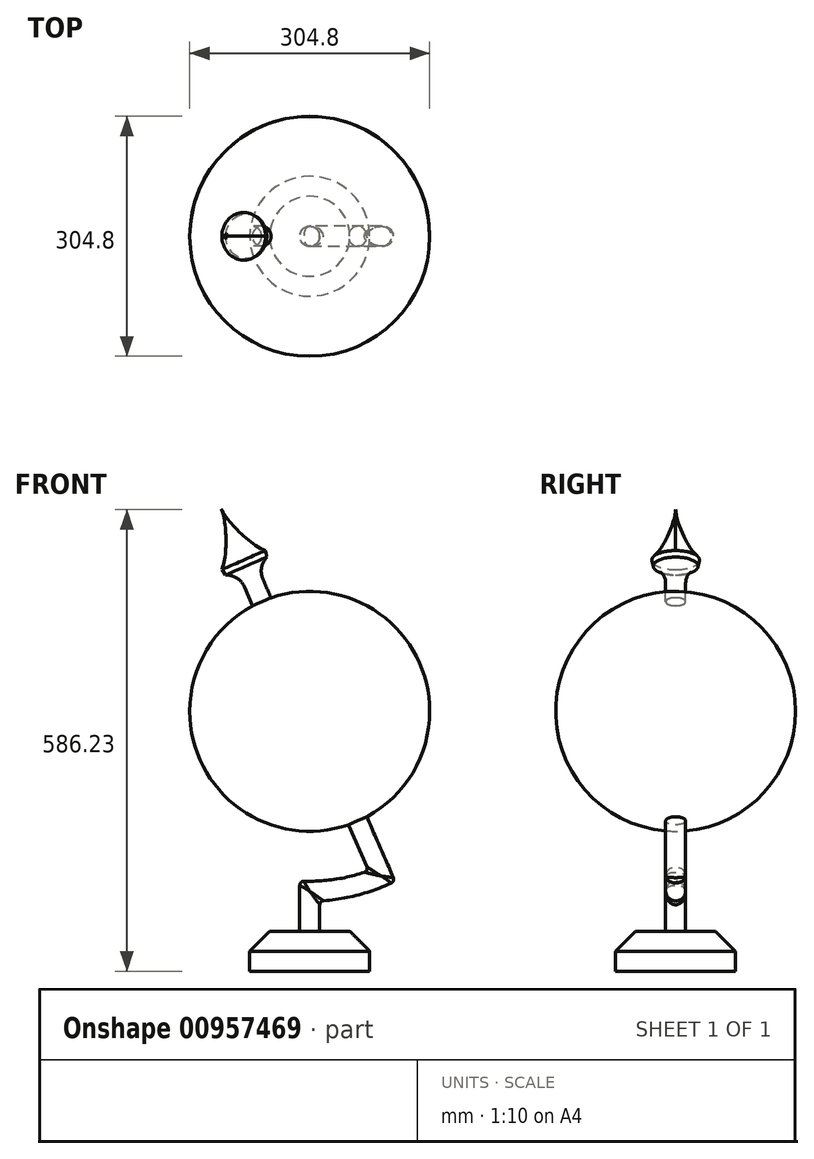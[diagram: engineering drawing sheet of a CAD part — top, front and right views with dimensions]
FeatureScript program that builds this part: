
annotation { "Feature Type Name" : "Feature", "Feature Type Description" : "" }
export const myFeature = defineFeature(function(context is Context, id is Id, definition is map)
    precondition{}
    {
        {
            var Q0;
            Q0=qCreatedBy(makeId("Front.planeOp"),FACE);
            var sketch = newSketch(context, id + "F0", { "sketchPlane" : qUnion([Q0])});
            skLineSegment(sketch, "E0", {"start": v(-152.4, 0) * mm, "end": v(152.4, 0) * mm});
            skArc(sketch, "E1", {"start": v(152.4, 0) * mm, "mid": v(0, 152.4) * mm, "end": v(-152.4, 0) * mm});
            skSolve(sketch);
        }
        {
            var Q0;
            Q0=makeQuery(id+"F0.imprint","IMPRINT",FACE,{"disambiguationData":[TD([[makeQuery(id+"F0.imprint","IMPRINT",EDGE,{"derivedFrom":sQuery(id+"F0.wireOp",EDGE,"E0")}),1.0]])]});
            var Q1;
            Q1=sQuery(id+"F0.wireOp",EDGE,"E0");
            revolve(context, id + "F1", {"surfaceOperationType" : NewSurfaceOperationType.NEW, "entities" : qUnion([Q0]), "axis" : qUnion([Q1]), "revolveType" : RevolveType.FULL});
        }
        {
            var Q0;
            Q0=qCreatedBy(makeId("Front.planeOp"),FACE);
            var sketch = newSketch(context, id + "F2", { "sketchPlane" : qUnion([Q0])});
            skLineSegment(sketch, "E2", {"start": v(0, 0) * mm, "end": v(0, 152.4) * mm, "construction": true});
            skLineSegment(sketch, "E3", {"start": v(-91.52, 209.48) * mm, "end": v(91.52, -209.48) * mm});
            skArc(sketch, "E4", {"start": v(91.52, -209.48) * mm, "mid": v(46.75, -223.77) * mm, "end": v(0, -228.6) * mm});
            skLineSegment(sketch, "E5", {"start": v(0, -228.6) * mm, "end": v(0, -330.2) * mm});
            skLineSegment(sketch, "E6.bottom", {"start": v(0, -330.2) * mm, "end": v(-76.2, -330.2) * mm});
            skLineSegment(sketch, "E6.top", {"start": v(0, -279.4) * mm, "end": v(-76.2, -279.4) * mm});
            skLineSegment(sketch, "E6.left", {"start": v(0, -330.2) * mm, "end": v(0, -279.4) * mm});
            skLineSegment(sketch, "E6.right", {"start": v(-76.2, -330.2) * mm, "end": v(-76.2, -279.4) * mm});
            skSolve(sketch);
        }
        {
            var Q0;
            Q0=makeQuery(id+"F2.imprint","IMPRINT",FACE,{"disambiguationData":[TD([[makeQuery(id+"F2.imprint","IMPRINT",EDGE,{"derivedFrom":sQuery(id+"F2.wireOp",EDGE,"E6.bottom")}),-1.0]])]});
            var Q1;
            Q1=sQuery(id+"F2.wireOp",EDGE,"E5");
            revolve(context, id + "F3", {"surfaceOperationType" : NewSurfaceOperationType.NEW, "entities" : qUnion([Q0]), "axis" : qUnion([Q1]), "revolveType" : RevolveType.FULL});
        }
        {
            var Q0;
            Q0=makeQuery(id+"F3.opRevolve","SWEPT_FACE",FACE,{"disambiguationData":[OSD([sQuery(id+"F2.wireOp",EDGE,"E6.top")])]});
            var sketch = newSketch(context, id + "F4", { "sketchPlane" : qUnion([Q0])});
            skCircle(sketch, "E7", {"center": v(0, 0) * mm, "radius": 12.7 * mm});
            skSolve(sketch);
        }
        {
            var Q0;
            Q0=makeQuery(id+"F4.imprint","IMPRINT",FACE,{"disambiguationData":[TD([[makeQuery(id+"F4.imprint","IMPRINT",EDGE,{"derivedFrom":sQuery(id+"F4.wireOp",EDGE,"E7")}),1.0]])]});
            var Q1;
            Q1=sQuery(id+"F2.wireOp",EDGE,"E5");
            var Q2;
            Q2=sQuery(id+"F2.wireOp",EDGE,"E4");
            var Q3;
            Q3=sQuery(id+"F2.wireOp",EDGE,"E3");
            sweep(context, id + "F5", {"operationType" : NewBodyOperationType.ADD, "profiles" : qUnion([Q0]), "path" : qUnion([Q1, Q2, Q3])});
        }
        {
            var Q0;
            Q0=qCreatedBy(makeId("Front.planeOp"),FACE);
            var sketch = newSketch(context, id + "F6", { "sketchPlane" : qUnion([Q0])});
            skLineSegment(sketch, "E8", {"start": v(-91.52, 209.48) * mm, "end": v(-111.86, 256.03) * mm});
            skFitSpline(sketch, "E9", {"points": [v(-111.86, 256.03) * mm, v(-46.44, 201.46) * mm], "startDerivative": vector(17.5, -40.06) * mm, "endDerivative": vector(75.42, -9.58) * mm});
            skLineSegment(sketch, "E10", {"start": v(-46.44, 201.46) * mm, "end": v(-81.35, 186.2) * mm});
            skLineSegment(sketch, "E11", {"start": v(-81.35, 186.2) * mm, "end": v(-91.52, 209.48) * mm});
            skSolve(sketch);
        }
        {
            var Q0;
            Q0=makeQuery(id+"F6.imprint","IMPRINT",FACE,{"disambiguationData":[TD([[makeQuery(id+"F6.imprint","IMPRINT",EDGE,{"derivedFrom":sQuery(id+"F6.wireOp",EDGE,"E8")}),-1.0]])]});
            var Q1;
            Q1=sQuery(id+"F6.wireOp",EDGE,"E8");
            revolve(context, id + "F7", {"operationType" : NewBodyOperationType.ADD, "surfaceOperationType" : NewSurfaceOperationType.NEW, "entities" : qUnion([Q0]), "axis" : qUnion([Q1]), "revolveType" : RevolveType.FULL});
        }
        {
            var Q0;
            Q0=makeQuery(id+"F7.boolean.opBoolean","INTERSECT",EDGE,{"derivedFrom":[makeQuery(id+"F5.opSweep","SWEPT_FACE",FACE,{"disambiguationData":[OSD([sQuery(id+"F2.wireOp",EDGE,"E3"),sQuery(id+"F4.wireOp",EDGE,"E7")])]}),makeQuery(id+"F7.opRevolve","SWEPT_FACE",FACE,{"disambiguationData":[OSD([sQuery(id+"F6.wireOp",EDGE,"E10")])]})]});
            fillet(context, id + "F8", {"entities" : qUnion([Q0]), "radius" : 25.4 * mm, "tangentPropagation" : true, "allowEdgeOverflow" : false});
        }
        {
            var Q0;
            Q0=makeQuery(id+"F3.opRevolve","SWEPT_EDGE",EDGE,{"disambiguationData":[OSD([sQuery(id+"F2.wireOp",EDGE,"E6.top"),sQuery(id+"F2.wireOp",EDGE,"E6.right")])]});
            chamfer(context, id + "F9", {"entities" : qUnion([Q0]), "width" : 25.4 * mm, "tangentPropagation" : true});
        }
        {
            var Q0;
            Q0=makeQuery(id+"F5.opSweep","MID_CAP_EDGE",EDGE,{"disambiguationData":[OSD([sQuery(id+"F2.wireOp",VERTEX,"E3.end"),sQuery(id+"F4.wireOp",EDGE,"E7")]),OD(1.0)],"capPos":2.0});
            var Q1;
            Q1=makeQuery(id+"F5.opSweep","MID_CAP_EDGE",EDGE,{"disambiguationData":[OSD([sQuery(id+"F2.wireOp",VERTEX,"E4.end"),sQuery(id+"F4.wireOp",EDGE,"E7")]),OD(0.0)],"capPos":1.0});
            var Q2;
            Q2=makeQuery(id+"F5.opSweep","MID_CAP_EDGE",EDGE,{"disambiguationData":[OSD([sQuery(id+"F2.wireOp",VERTEX,"E4.end"),sQuery(id+"F4.wireOp",EDGE,"E7")]),OD(1.0)],"capPos":1.0});
            var Q3;
            Q3=makeQuery(id+"F5.opSweep","MID_CAP_EDGE",EDGE,{"disambiguationData":[OSD([sQuery(id+"F2.wireOp",VERTEX,"E3.end"),sQuery(id+"F4.wireOp",EDGE,"E7")]),OD(0.0)],"capPos":2.0});
            fillet(context, id + "F10", {"entities" : qUnion([Q0, Q1, Q2, Q3]), "radius" : 5.08 * mm, "tangentPropagation" : true, "allowEdgeOverflow" : false});
        }
        {
            var Q0;
            Q0=makeQuery(id+"F8.opFillet","BLEND_EDGE",EDGE,{"blendedFrom":[makeQuery(id+"F7.boolean.opBoolean","INTERSECT",EDGE,{"derivedFrom":[makeQuery(id+"F5.opSweep","SWEPT_FACE",FACE,{"disambiguationData":[OSD([sQuery(id+"F2.wireOp",EDGE,"E3"),sQuery(id+"F4.wireOp",EDGE,"E7")])]}),makeQuery(id+"F7.opRevolve","SWEPT_FACE",FACE,{"disambiguationData":[OSD([sQuery(id+"F6.wireOp",EDGE,"E10")])]})]}),makeQuery(id+"F7.opRevolve","SWEPT_FACE",FACE,{"disambiguationData":[OSD([sQuery(id+"F6.wireOp",EDGE,"E9")])]})],"blendedInto":[makeQuery(id+"F7.opRevolve","SWEPT_FACE",FACE,{"disambiguationData":[OSD([sQuery(id+"F6.wireOp",EDGE,"E9")])]})]});
            chamfer(context, id + "F11", {"entities" : qUnion([Q0]), "width" : 5.08 * mm, "tangentPropagation" : true});
        }
    });
